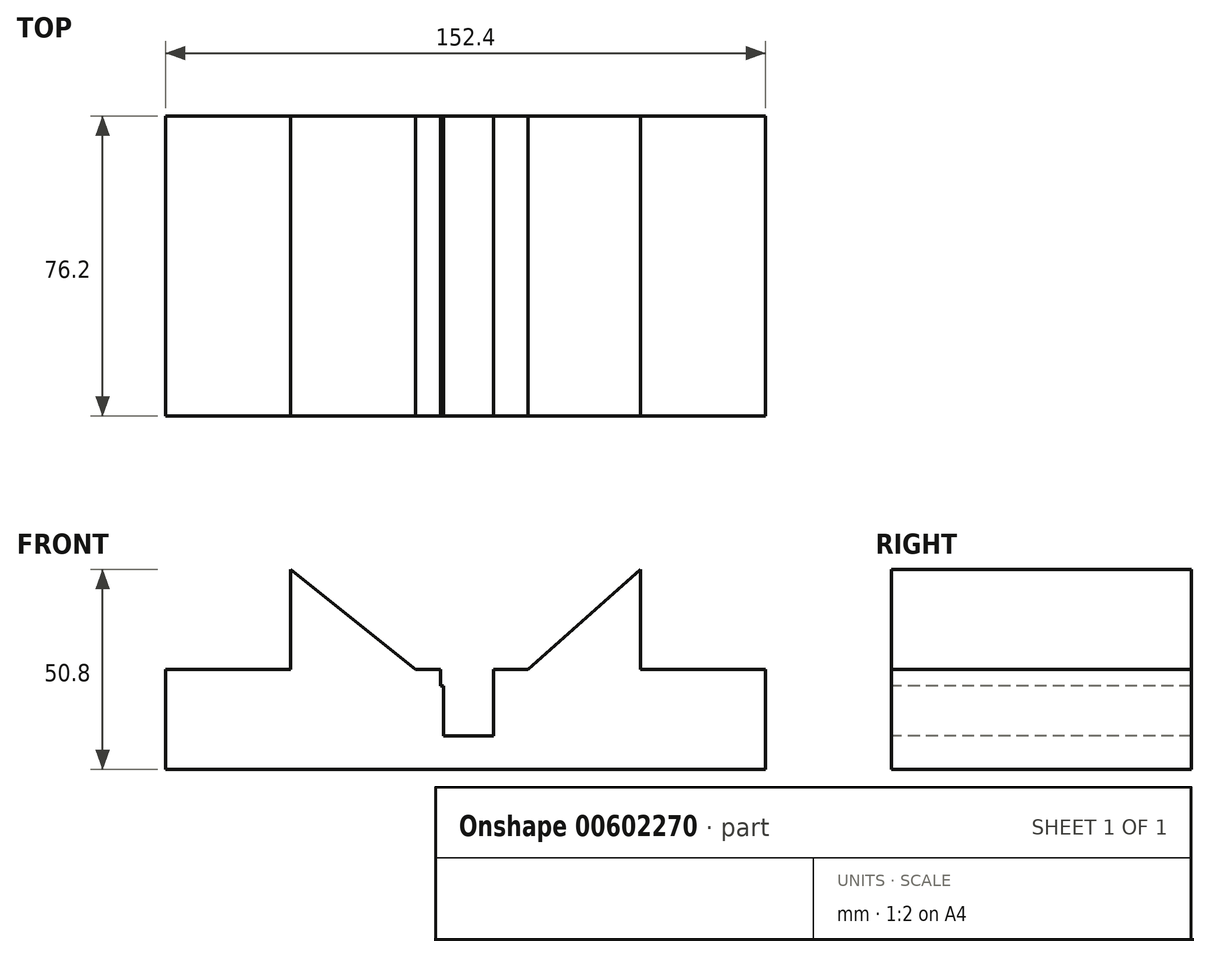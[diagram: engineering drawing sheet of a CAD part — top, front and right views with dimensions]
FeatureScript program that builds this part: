
annotation { "Feature Type Name" : "Feature", "Feature Type Description" : "" }
export const myFeature = defineFeature(function(context is Context, id is Id, definition is map)
    precondition{}
    {
        {
            var Q0;
            Q0=qCreatedBy(makeId("Front.planeOp"),FACE);
            var sketch = newSketch(context, id + "F0", { "sketchPlane" : qUnion([Q0])});
            skLineSegment(sketch, "E0.bottom", {"start": v(-76.58, -23.83) * mm, "end": v(75.82, -23.83) * mm});
            skLineSegment(sketch, "E0.top", {"start": v(-76.58, -74.63) * mm, "end": v(75.82, -74.63) * mm});
            skLineSegment(sketch, "E0.left", {"start": v(-76.58, -23.83) * mm, "end": v(-76.58, -74.63) * mm});
            skLineSegment(sketch, "E0.right", {"start": v(75.82, -23.83) * mm, "end": v(75.82, -74.63) * mm});
            skSolve(sketch);
        }
        {
            var Q0;
            Q0=makeQuery(id+"F0.imprint","IMPRINT",FACE,{"disambiguationData":[TD([[makeQuery(id+"F0.imprint","IMPRINT",EDGE,{"derivedFrom":sQuery(id+"F0.wireOp",EDGE,"E0.bottom")}),-1.0]])]});
            extrude(context, id + "F1", {"entities" : qUnion([Q0]), "oppositeDirection" : true, "depth" : 76.2 * mm, "offsetDistance" : 25.4 * mm});
        }
        {
            var Q0;
            Q0=makeQuery(id+"F1.opExtrude","CAP_FACE",FACE,{"disambiguationData":[OSD([sQuery(id+"F0.wireOp",EDGE,"E0.bottom"),sQuery(id+"F0.wireOp",EDGE,"E0.top"),sQuery(id+"F0.wireOp",EDGE,"E0.left"),sQuery(id+"F0.wireOp",EDGE,"E0.right")])],"isStart":true});
            var sketch = newSketch(context, id + "F2", { "sketchPlane" : qUnion([Q0])});
            skLineSegment(sketch, "E1.bottom", {"start": v(-76.58, -23.83) * mm, "end": v(-44.83, -23.83) * mm});
            skLineSegment(sketch, "E1.top", {"start": v(-76.58, -49.23) * mm, "end": v(-44.83, -49.23) * mm});
            skLineSegment(sketch, "E1.left", {"start": v(-76.58, -23.83) * mm, "end": v(-76.58, -49.23) * mm});
            skLineSegment(sketch, "E1.right", {"start": v(-44.83, -23.83) * mm, "end": v(-44.83, -49.23) * mm});
            skSolve(sketch);
        }
        {
            var Q0;
            Q0=makeQuery(id+"F2.imprint","IMPRINT",FACE,{"disambiguationData":[TD([[makeQuery(id+"F2.imprint","IMPRINT",EDGE,{"derivedFrom":sQuery(id+"F2.wireOp",EDGE,"E1.bottom")}),-1.0]])]});
            extrude(context, id + "F3", {"entities" : qUnion([Q0]), "operationType" : NewBodyOperationType.REMOVE, "oppositeDirection" : true, "depth" : 76.2 * mm, "offsetDistance" : 25.4 * mm});
        }
        {
            var Q0;
            Q0=makeQuery(id+"F1.opExtrude","CAP_FACE",FACE,{"disambiguationData":[OSD([sQuery(id+"F0.wireOp",EDGE,"E0.bottom"),sQuery(id+"F0.wireOp",EDGE,"E0.top"),sQuery(id+"F0.wireOp",EDGE,"E0.left"),sQuery(id+"F0.wireOp",EDGE,"E0.right")])],"isStart":true});
            var sketch = newSketch(context, id + "F4", { "sketchPlane" : qUnion([Q0])});
            skLineSegment(sketch, "E2.bottom", {"start": v(75.82, -23.83) * mm, "end": v(44.07, -23.83) * mm});
            skLineSegment(sketch, "E2.top", {"start": v(75.82, -49.23) * mm, "end": v(44.07, -49.23) * mm});
            skLineSegment(sketch, "E2.left", {"start": v(75.82, -23.83) * mm, "end": v(75.82, -49.23) * mm});
            skLineSegment(sketch, "E2.right", {"start": v(44.07, -23.83) * mm, "end": v(44.07, -49.23) * mm});
            skSolve(sketch);
        }
        {
            var Q0;
            Q0=makeQuery(id+"F4.imprint","IMPRINT",FACE,{"disambiguationData":[TD([[makeQuery(id+"F4.imprint","IMPRINT",EDGE,{"derivedFrom":sQuery(id+"F4.wireOp",EDGE,"E2.bottom")}),-1.0]])]});
            extrude(context, id + "F5", {"entities" : qUnion([Q0]), "operationType" : NewBodyOperationType.REMOVE, "oppositeDirection" : true, "depth" : 76.2 * mm, "offsetDistance" : 25.4 * mm});
        }
        {
            var Q0;
            Q0=makeQuery(id+"F1.opExtrude","CAP_FACE",FACE,{"disambiguationData":[OSD([sQuery(id+"F0.wireOp",EDGE,"E0.bottom"),sQuery(id+"F0.wireOp",EDGE,"E0.top"),sQuery(id+"F0.wireOp",EDGE,"E0.left"),sQuery(id+"F0.wireOp",EDGE,"E0.right")])],"isStart":true});
            var sketch = newSketch(context, id + "F6", { "sketchPlane" : qUnion([Q0])});
            skLineSegment(sketch, "E3", {"start": v(-44.83, -23.83) * mm, "end": v(-13.08, -23.83) * mm});
            skLineSegment(sketch, "E4", {"start": v(-13.08, -23.83) * mm, "end": v(-13.08, -49.23) * mm});
            skLineSegment(sketch, "E5", {"start": v(-13.08, -49.23) * mm, "end": v(-44.83, -23.83) * mm});
            skSolve(sketch);
        }
        {
            var Q0;
            Q0=makeQuery(id+"F6.imprint","IMPRINT",FACE,{"disambiguationData":[TD([[makeQuery(id+"F6.imprint","IMPRINT",EDGE,{"derivedFrom":sQuery(id+"F6.wireOp",EDGE,"E3")}),-1.0]])]});
            extrude(context, id + "F7", {"entities" : qUnion([Q0]), "operationType" : NewBodyOperationType.REMOVE, "oppositeDirection" : true, "depth" : 76.2 * mm, "offsetDistance" : 25.4 * mm});
        }
        {
            var Q0;
            Q0=makeQuery(id+"F1.opExtrude","CAP_FACE",FACE,{"disambiguationData":[OSD([sQuery(id+"F0.wireOp",EDGE,"E0.bottom"),sQuery(id+"F0.wireOp",EDGE,"E0.top"),sQuery(id+"F0.wireOp",EDGE,"E0.left"),sQuery(id+"F0.wireOp",EDGE,"E0.right")])],"isStart":true});
            var sketch = newSketch(context, id + "F8", { "sketchPlane" : qUnion([Q0])});
            skLineSegment(sketch, "E6", {"start": v(15.5, -23.83) * mm, "end": v(15.5, -49.23) * mm});
            skLineSegment(sketch, "E7", {"start": v(15.5, -49.23) * mm, "end": v(44.07, -23.83) * mm});
            skLineSegment(sketch, "E8", {"start": v(44.07, -23.83) * mm, "end": v(15.5, -23.83) * mm});
            skSolve(sketch);
        }
        {
            var Q0;
            Q0 = qSketchRegion(id + "F8", true);
            extrude(context, id + "F9", {"entities" : qUnion([Q0]), "operationType" : NewBodyOperationType.REMOVE, "oppositeDirection" : true, "depth" : 76.2 * mm, "offsetDistance" : 25.4 * mm});
        }
        {
            var Q0;
            Q0=makeQuery(id+"F1.opExtrude","CAP_FACE",FACE,{"disambiguationData":[OSD([sQuery(id+"F0.wireOp",EDGE,"E0.bottom"),sQuery(id+"F0.wireOp",EDGE,"E0.top"),sQuery(id+"F0.wireOp",EDGE,"E0.left"),sQuery(id+"F0.wireOp",EDGE,"E0.right")])],"isStart":true});
            var sketch = newSketch(context, id + "F10", { "sketchPlane" : qUnion([Q0])});
            skLineSegment(sketch, "E9.bottom", {"start": v(-13.08, -49.23) * mm, "end": v(15.5, -49.23) * mm});
            skLineSegment(sketch, "E9.top", {"start": v(-13.08, -23.83) * mm, "end": v(15.5, -23.83) * mm});
            skLineSegment(sketch, "E9.left", {"start": v(-13.08, -49.23) * mm, "end": v(-13.08, -23.83) * mm});
            skLineSegment(sketch, "E9.right", {"start": v(15.5, -49.23) * mm, "end": v(15.5, -23.83) * mm});
            skSolve(sketch);
        }
        {
            var Q0;
            Q0=makeQuery(id+"F10.imprint","IMPRINT",FACE,{"disambiguationData":[TD([[makeQuery(id+"F10.imprint","IMPRINT",EDGE,{"derivedFrom":sQuery(id+"F10.wireOp",EDGE,"E9.bottom")}),1.0]])]});
            extrude(context, id + "F11", {"entities" : qUnion([Q0]), "operationType" : NewBodyOperationType.REMOVE, "oppositeDirection" : true, "depth" : 76.2 * mm, "offsetDistance" : 25.4 * mm});
        }
        {
            var Q0;
            Q0=makeQuery(id+"F1.opExtrude","CAP_FACE",FACE,{"disambiguationData":[OSD([sQuery(id+"F0.wireOp",EDGE,"E0.bottom"),sQuery(id+"F0.wireOp",EDGE,"E0.top"),sQuery(id+"F0.wireOp",EDGE,"E0.left"),sQuery(id+"F0.wireOp",EDGE,"E0.right")])],"isStart":true});
            var sketch = newSketch(context, id + "F12", { "sketchPlane" : qUnion([Q0])});
            skLineSegment(sketch, "E10.bottom", {"start": v(-6.01, -53.37) * mm, "end": v(6.69, -53.37) * mm});
            skLineSegment(sketch, "E10.top", {"start": v(-6.01, -66.07) * mm, "end": v(6.69, -66.07) * mm});
            skLineSegment(sketch, "E10.left", {"start": v(-6.01, -53.37) * mm, "end": v(-6.01, -66.07) * mm});
            skLineSegment(sketch, "E10.right", {"start": v(6.69, -53.37) * mm, "end": v(6.69, -66.07) * mm});
            skSolve(sketch);
        }
        {
            var Q0;
            Q0 = qSketchRegion(id + "F12", true);
            extrude(context, id + "F13", {"entities" : qUnion([Q0]), "operationType" : NewBodyOperationType.REMOVE, "oppositeDirection" : true, "depth" : 101.6 * mm, "offsetDistance" : 25.4 * mm});
        }
        {
            var Q0;
            Q0=makeQuery(id+"F1.opExtrude","CAP_FACE",FACE,{"disambiguationData":[OSD([sQuery(id+"F0.wireOp",EDGE,"E0.bottom"),sQuery(id+"F0.wireOp",EDGE,"E0.top"),sQuery(id+"F0.wireOp",EDGE,"E0.left"),sQuery(id+"F0.wireOp",EDGE,"E0.right")])],"isStart":true});
            var sketch = newSketch(context, id + "F14", { "sketchPlane" : qUnion([Q0])});
            skLineSegment(sketch, "E11.bottom", {"start": v(-6.67, -49.23) * mm, "end": v(6.69, -49.23) * mm});
            skLineSegment(sketch, "E11.top", {"start": v(-6.67, -53.37) * mm, "end": v(6.69, -53.37) * mm});
            skLineSegment(sketch, "E11.left", {"start": v(-6.67, -49.23) * mm, "end": v(-6.67, -53.37) * mm});
            skLineSegment(sketch, "E11.right", {"start": v(6.69, -49.23) * mm, "end": v(6.69, -53.37) * mm});
            skSolve(sketch);
        }
        {
            var Q0;
            Q0=makeQuery(id+"F14.imprint","IMPRINT",FACE,{"disambiguationData":[TD([[makeQuery(id+"F14.imprint","IMPRINT",EDGE,{"derivedFrom":sQuery(id+"F14.wireOp",EDGE,"E11.bottom")}),-1.0]])]});
            extrude(context, id + "F15", {"entities" : qUnion([Q0]), "operationType" : NewBodyOperationType.REMOVE, "oppositeDirection" : true, "depth" : 101.6 * mm, "offsetDistance" : 25.4 * mm});
        }
    });
